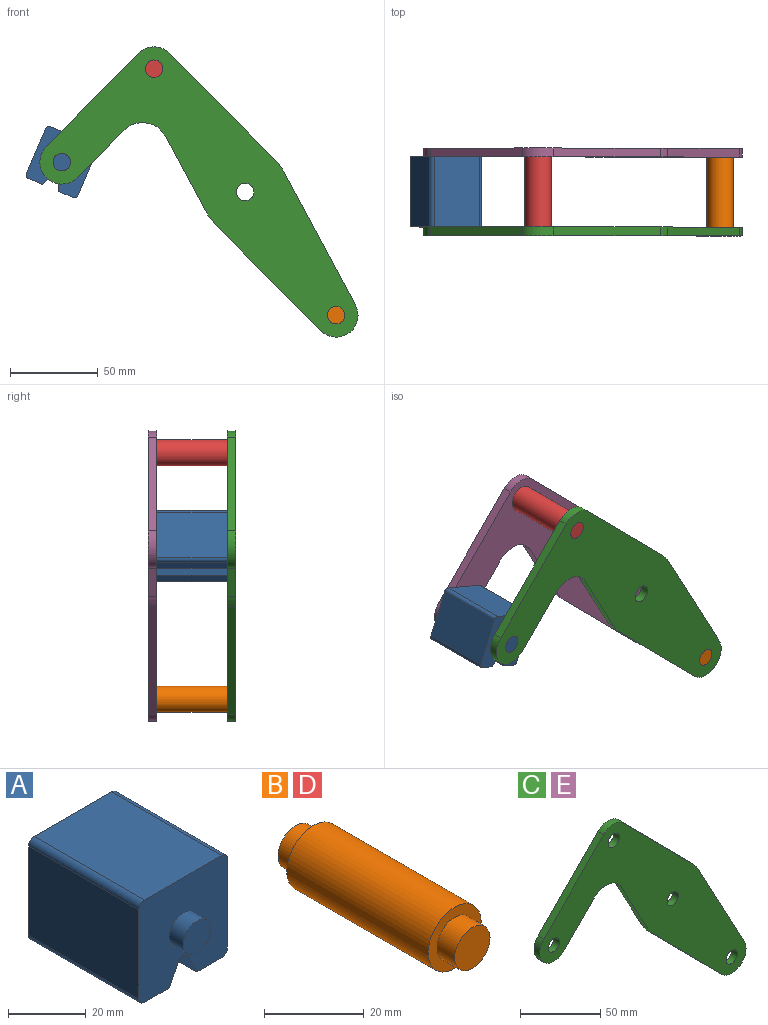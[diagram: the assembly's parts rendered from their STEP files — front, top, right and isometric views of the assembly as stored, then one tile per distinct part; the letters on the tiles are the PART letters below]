
ASSEMBLY  parts=5 mates=3
PART A: 18 faces, bbox 32.1x50x32.1 mm
  f0: plane 40x28.08mm, normal (1,0,0), area 1123.1mm2, adj f4,f10,f13,f14
  f1: plane 40x9.04mm, normal (0,0,-1), area 361.6mm2, adj f2,f4,f10,f14
  f2: plane 40x6.42mm, normal (-0.89,0,-0.45), area 287.2mm2, adj f1,f4,f10,f15
  f3: plane 40x6.42mm, normal (0.89,0,-0.45), area 287.2mm2, adj f4,f5,f10,f15
  f4: plane 32.08x32.08mm, normal (0,-1,0), area 900.6mm2, adj f0,f1,f2,f3,f5,f6,f7,f9
  f5: plane 40x9.04mm, normal (0,0,-1), area 361.6mm2, adj f3,f4,f10,f16
  f6: plane 40x28.08mm, normal (0,0,1), area 1123.1mm2, adj f4,f10,f13,f17
  f7: plane 40x28.08mm, normal (-1,0,0), area 1123.1mm2, adj f4,f10,f16,f17
  f8: plane 10x10mm, normal (0,-1,0), area 78.5mm2, adj f9
  f9: cylinder r=5mm len=10mm, axis (0,1,0), area 157.1mm2, adj f4,f8
  f10: plane 32.08x32.08mm, normal (0,1,0), area 900.6mm2, adj f0,f1,f2,f3,f5,f6,f7,f12
  f11: plane 10x10mm, normal (0,1,0), area 78.5mm2, adj f12
  f12: cylinder r=5mm len=10mm, axis (0,-1,0), area 157.1mm2, adj f10,f11
  f13: cylinder r=2mm len=40mm, axis (0,1,0), area 125.7mm2, adj f0,f4,f6,f10
  f14: cylinder r=2mm len=40mm, axis (0,-1,0), area 125.7mm2, adj f0,f1,f4,f10
  f15: cylinder r=2mm len=40mm, axis (0,1,0), area 177.1mm2, adj f2,f3,f4,f10
  f16: cylinder r=2mm len=40mm, axis (0,1,0), area 125.7mm2, adj f4,f5,f7,f10
  f17: cylinder r=2mm len=40mm, axis (0,-1,0), area 125.7mm2, adj f4,f6,f7,f10
PART B: 7 faces, bbox 15x50x15 mm
  f0: cylinder r=7.5mm len=40mm, axis (0,-1,0), area 1885mm2, adj f2,f5
  f1: cylinder r=5mm len=10mm, axis (0,1,0), area 157.1mm2, adj f2,f3
  f2: plane 15x15mm, normal (0,-1,0), area 98.2mm2, adj f0,f1
  f3: plane 10x10mm, normal (0,-1,0), area 78.5mm2, adj f1
  f4: cylinder r=5mm len=10mm, axis (0,-1,0), area 157.1mm2, adj f5,f6
  f5: plane 15x15mm, normal (0,1,0), area 98.2mm2, adj f0,f4
  f6: plane 10x10mm, normal (0,1,0), area 78.5mm2, adj f4
PART C: 18 faces, bbox 181.7x5x165.8 mm
  f0: plane 43.49x23.35mm, normal (-0.88,0,-0.47), area 246.8mm2, adj f1,f14,f16,f17
  f1: cylinder r=25mm len=5.75mm, axis (0,1,0), area 35.8mm2, adj f0,f2,f16,f17
  f2: plane 61.6x60.87mm, normal (-0.71,0,-0.7), area 433mm2, adj f1,f3,f16,f17
  f3: cylinder r=12.5mm len=21.39mm, axis (0,1,0), area 178.4mm2, adj f2,f4,f16,f17
  f4: plane 76.3x40.96mm, normal (0.88,0,0.47), area 433mm2, adj f3,f5,f16,f17
  f5: cylinder r=25mm len=5.75mm, axis (0,1,0), area 35.8mm2, adj f4,f6,f16,f17
  f6: plane 61.6x60.87mm, normal (0.71,0,0.7), area 433mm2, adj f5,f7,f16,f17
  f7: cylinder r=12.5mm len=17.78mm, axis (0,1,0), area 98.9mm2, adj f6,f8,f16,f17
  f8: plane 53.35x52.71mm, normal (-0.71,0,0.7), area 375mm2, adj f7,f9,f16,f17
  f9: cylinder r=12.5mm len=21.39mm, axis (0,1,0), area 196.3mm2, adj f8,f10,f16,f17
  f10: plane 26.86x26.54mm, normal (0.71,0,-0.7), area 188.8mm2, adj f9,f14,f16,f17
  f11: cylinder r=5mm len=10mm, axis (0,1,0), area 157.1mm2, adj f16,f17
  f12: cylinder r=5mm len=10mm, axis (0,1,0), area 157.1mm2, adj f16,f17
  f13: cylinder r=5mm len=10mm, axis (0,1,0), area 157.1mm2, adj f16,f17
  f14: cylinder r=15mm len=23.89mm, axis (0,1,0), area 140.2mm2, adj f0,f10,f16,f17
  f15: cylinder r=5mm len=10mm, axis (0,1,0), area 157.1mm2, adj f16,f17
  f16: plane 181.66x165.78mm, normal (0,-1,0), area 8710.1mm2, adj f0,f1,f2,f3,f4,f5,f6,f7
  f17: plane 181.66x165.78mm, normal (0,1,0), area 8710.1mm2, adj f0,f1,f2,f3,f4,f5,f6,f7
PART D: same geometry as B
PART E: same geometry as C
PLACE A rot(axis=(0,1,0),23.3deg) t=(-99.02,-78.82,-29.31)mm
PLACE B t=(20.24,-78.82,-130.04)mm
PLACE C t=(-83.71,-78.82,10.75)mm fixed
PLACE D t=(-83.71,-78.82,10.75)mm
PLACE E t=(-83.71,-33.82,10.75)mm
MATE revolute D.f0 <-> E.f7  axis (0,1,0) through (-135.69,-38.82,81.14)mm
MATE revolute A.f9 <-> C.f9  axis (0,-1,0) through (-188.4,-78.82,27.78)mm
MATE fastened B.f0 <-> C.f3  axis (0,1,0) through (-31.74,-78.82,-59.65)mm
